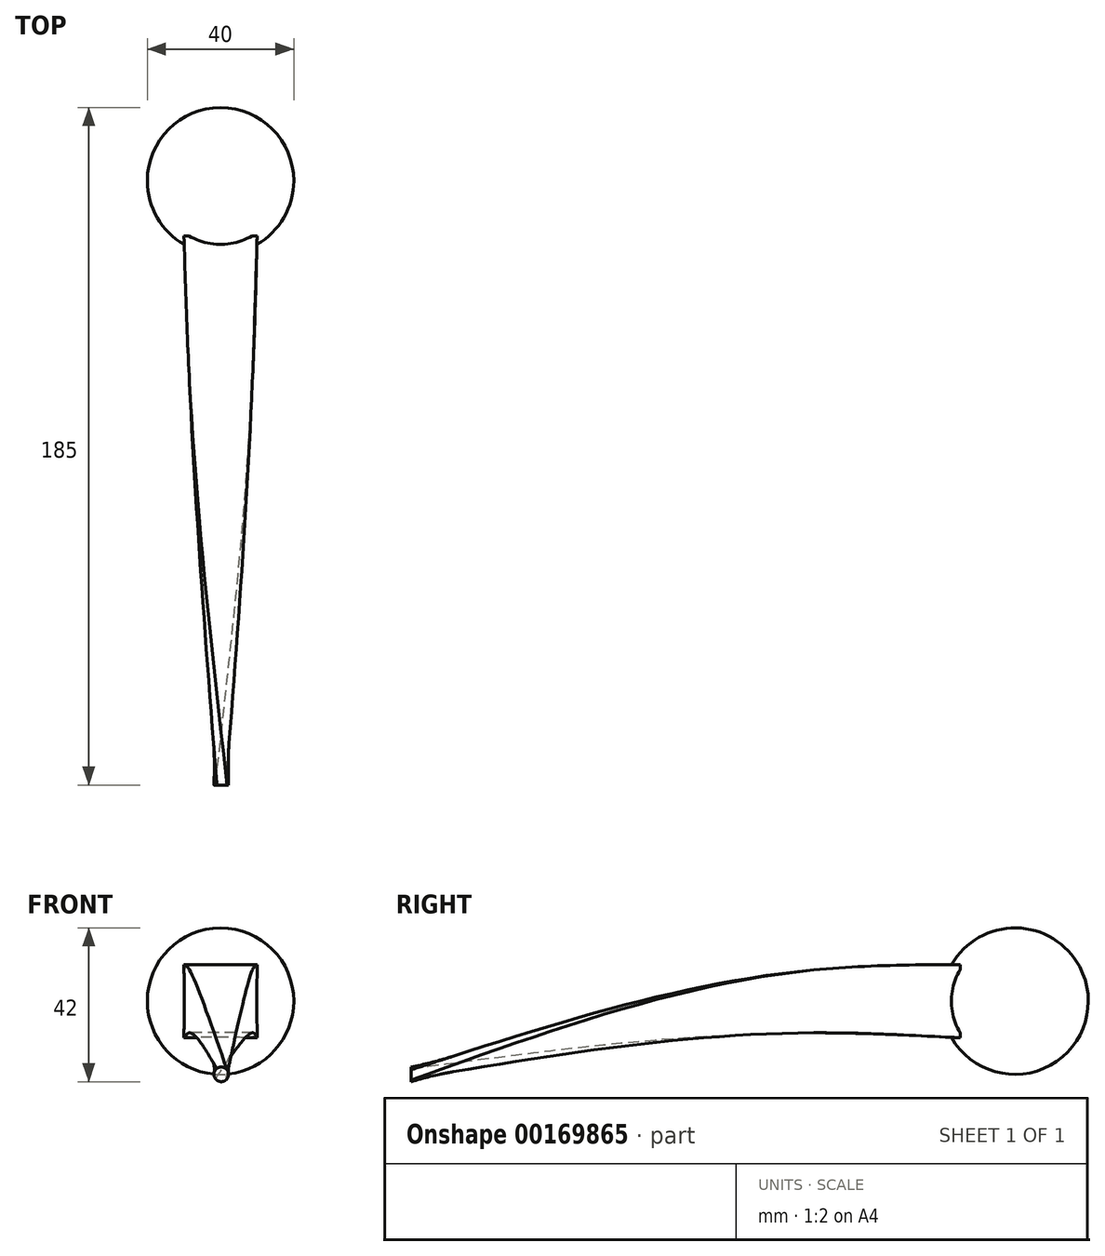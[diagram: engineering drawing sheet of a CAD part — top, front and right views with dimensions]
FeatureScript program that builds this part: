
annotation { "Feature Type Name" : "Feature", "Feature Type Description" : "" }
export const myFeature = defineFeature(function(context is Context, id is Id, definition is map)
    precondition{}
    {
        {
            var Q0;
            Q0=qCreatedBy(makeId("Front.planeOp"),FACE);
            cPlane(context, id + "F0", {"entities" : qUnion([Q0]), "cplaneType" : CPlaneType.OFFSET, "offset" : 15 * mm, "width" : 150 * mm, "height" : 150 * mm});
        }
        {
            var Q0;
            Q0=qCreatedBy(makeId("Front.planeOp"),FACE);
            var sketch = newSketch(context, id + "F1", { "sketchPlane" : qUnion([Q0])});
            skLineSegment(sketch, "E0", {"start": v(-20, 0) * mm, "end": v(20, 0) * mm});
            skArc(sketch, "E1", {"start": v(20, 0) * mm, "mid": v(0, 20) * mm, "end": v(-20, 0) * mm});
            skPoint(sketch, "E2.orphan", {"position": v(-18.89, 0) * mm});
            skSolve(sketch);
        }
        {
            var Q0;
            Q0=makeQuery(id+"F1.imprint","IMPRINT",FACE,{"disambiguationData":[TD([[makeQuery(id+"F1.imprint","IMPRINT",EDGE,{"derivedFrom":sQuery(id+"F1.wireOp",EDGE,"E0")}),1.0]])]});
            var Q1;
            Q1=sQuery(id+"F1.wireOp",EDGE,"E0");
            revolve(context, id + "F2", {"entities" : qUnion([Q0]), "axis" : qUnion([Q1]), "revolveType" : RevolveType.FULL});
        }
        {
            var Q0;
            Q0=qCreatedBy(id+"F0.planeOp",FACE);
            var sketch = newSketch(context, id + "F3", { "sketchPlane" : qUnion([Q0])});
            skLineSegment(sketch, "E3.bottom", {"start": v(-10, -10) * mm, "end": v(10, -10) * mm});
            skLineSegment(sketch, "E3.top", {"start": v(-10, 10) * mm, "end": v(10, 10) * mm});
            skLineSegment(sketch, "E3.left", {"start": v(-10, -10) * mm, "end": v(-10, 10) * mm});
            skLineSegment(sketch, "E3.right", {"start": v(10, -10) * mm, "end": v(10, 10) * mm});
            skPoint(sketch, "E3.middle", {"position": v(0, 0) * mm});
            skSolve(sketch);
        }
        {
            var Q0;
            Q0=qCreatedBy(id+"F0.planeOp",FACE);
            cPlane(context, id + "F4", {"entities" : qUnion([Q0]), "cplaneType" : CPlaneType.OFFSET, "offset" : 150 * mm, "width" : 150 * mm, "height" : 150 * mm});
        }
        {
            var Q0;
            Q0=qCreatedBy(id+"F0.planeOp",FACE);
            cPlane(context, id + "F5", {"entities" : qUnion([Q0]), "cplaneType" : CPlaneType.OFFSET, "offset" : 40 * mm, "width" : 150 * mm, "height" : 150 * mm});
        }
        {
            var Q0;
            Q0=qCreatedBy(id+"F5.planeOp",FACE);
            var sketch = newSketch(context, id + "F6", { "sketchPlane" : qUnion([Q0])});
            skLineSegment(sketch, "E4.bottom", {"start": v(-8.47, -8.64) * mm, "end": v(8.68, -8.64) * mm});
            skLineSegment(sketch, "E4.top", {"start": v(-8.47, 8.5) * mm, "end": v(8.68, 8.5) * mm});
            skLineSegment(sketch, "E4.left", {"start": v(-8.47, -8.64) * mm, "end": v(-8.47, 8.5) * mm});
            skLineSegment(sketch, "E4.right", {"start": v(8.68, -8.64) * mm, "end": v(8.68, 8.5) * mm});
            skPoint(sketch, "E4.middle", {"position": v(0.1, -0.07) * mm});
            skSolve(sketch);
        }
        {
            var Q0;
            Q0=qCreatedBy(id+"F4.planeOp",FACE);
            var sketch = newSketch(context, id + "F7", { "sketchPlane" : qUnion([Q0])});
            skCircle(sketch, "E5", {"center": v(0.2, -20) * mm, "radius": 2 * mm});
            skSolve(sketch);
        }
        {
            var Q0;
            Q0=makeQuery(id+"F7.imprint","IMPRINT",FACE,{"disambiguationData":[TD([[makeQuery(id+"F7.imprint","IMPRINT",EDGE,{"derivedFrom":sQuery(id+"F7.wireOp",EDGE,"E5")}),1.0]])]});
            var Q1;
            Q1=makeQuery(id+"F6.imprint","IMPRINT",FACE,{"disambiguationData":[TD([[makeQuery(id+"F6.imprint","IMPRINT",EDGE,{"derivedFrom":sQuery(id+"F6.wireOp",EDGE,"E4.bottom")}),1.0]])]});
            var Q2;
            Q2=makeQuery(id+"F3.imprint","IMPRINT",FACE,{"disambiguationData":[TD([[makeQuery(id+"F3.imprint","IMPRINT",EDGE,{"derivedFrom":sQuery(id+"F3.wireOp",EDGE,"E3.bottom")}),1.0]])]});
            loft(context, id + "F8", {"operationType" : NewBodyOperationType.ADD, "sheetProfilesArray" : [{ "sheetProfileEntities" : qUnion([Q0]) }, { "sheetProfileEntities" : qUnion([Q1]) }, { "sheetProfileEntities" : qUnion([Q2]) }]});
        }
    });
